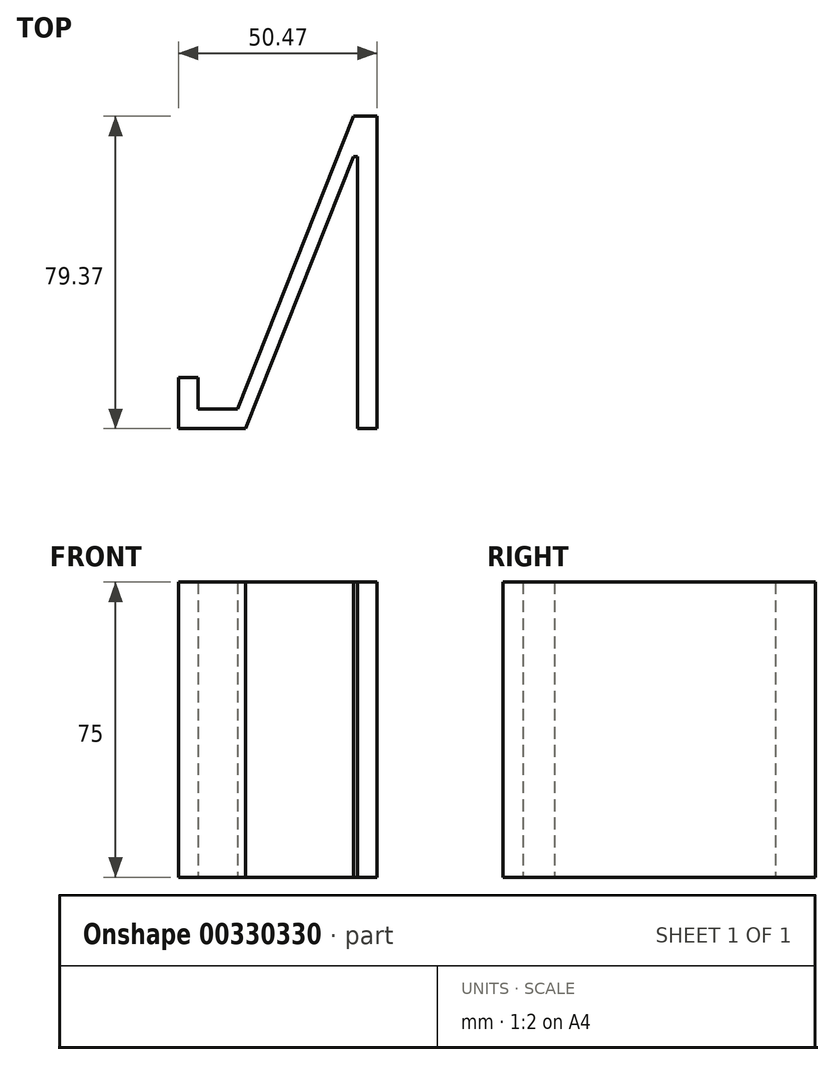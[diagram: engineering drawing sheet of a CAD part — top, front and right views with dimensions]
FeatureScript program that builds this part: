
annotation { "Feature Type Name" : "Feature", "Feature Type Description" : "" }
export const myFeature = defineFeature(function(context is Context, id is Id, definition is map)
    precondition{}
    {
        {
            var Q0;
            Q0=qCreatedBy(makeId("Top.planeOp"),FACE);
            var sketch = newSketch(context, id + "F0", { "sketchPlane" : qUnion([Q0])});
            skLineSegment(sketch, "E0", {"start": v(0, 0) * mm, "end": v(0, 13) * mm});
            skLineSegment(sketch, "E1", {"start": v(0, 13) * mm, "end": v(5, 13) * mm});
            skLineSegment(sketch, "E2", {"start": v(5, 13) * mm, "end": v(5, 5) * mm});
            skLineSegment(sketch, "E3", {"start": v(5, 5) * mm, "end": v(15, 5) * mm});
            skLineSegment(sketch, "E4", {"start": v(15, 5) * mm, "end": v(44.47, 79.37) * mm});
            skLineSegment(sketch, "E5", {"start": v(44.47, 79.37) * mm, "end": v(50.47, 79.37) * mm});
            skLineSegment(sketch, "E6", {"start": v(50.47, 79.37) * mm, "end": v(50.47, 0) * mm});
            skLineSegment(sketch, "E7", {"start": v(50.47, 0) * mm, "end": v(45.47, 0) * mm});
            skLineSegment(sketch, "E8", {"start": v(45.47, 0) * mm, "end": v(45.47, 69.16) * mm});
            skLineSegment(sketch, "E9", {"start": v(45.47, 69.16) * mm, "end": v(44.47, 69.16) * mm});
            skLineSegment(sketch, "E10", {"start": v(44.47, 69.16) * mm, "end": v(17.07, 0) * mm});
            skLineSegment(sketch, "E11", {"start": v(17.07, 0) * mm, "end": v(0, 0) * mm});
            skSolve(sketch);
        }
        {
            var Q0;
            Q0=makeQuery(id+"F0.imprint","IMPRINT",FACE,{"disambiguationData":[TD([[makeQuery(id+"F0.imprint","IMPRINT",EDGE,{"derivedFrom":sQuery(id+"F0.wireOp",EDGE,"E0")}),-1.0]])]});
            extrude(context, id + "F1", {"entities" : qUnion([Q0]), "depth" : 75 * mm});
        }
    });
